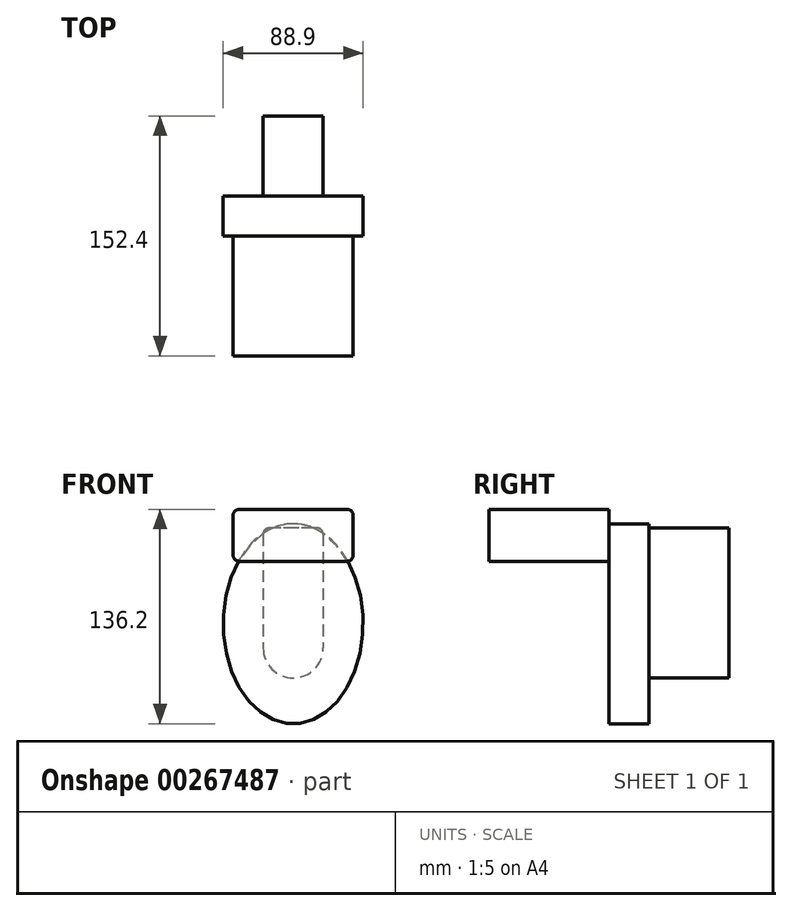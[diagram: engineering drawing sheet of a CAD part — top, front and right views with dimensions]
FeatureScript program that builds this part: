
annotation { "Feature Type Name" : "Feature", "Feature Type Description" : "" }
export const myFeature = defineFeature(function(context is Context, id is Id, definition is map)
    precondition{}
    {
        {
            var Q0;
            Q0=qCreatedBy(makeId("Front.planeOp"),FACE);
            var sketch = newSketch(context, id + "F0", { "sketchPlane" : qUnion([Q0])});
            skLineSegment(sketch, "E0.bottom", {"start": v(15.24, 36.63) * mm, "end": v(-15.24, 36.63) * mm});
            skLineSegment(sketch, "E0.top", {"start": v(19.05, -39.57) * mm, "end": v(-19.05, -39.57) * mm});
            skLineSegment(sketch, "E0.left", {"start": v(19.05, 32.82) * mm, "end": v(19.05, -39.57) * mm});
            skLineSegment(sketch, "E0.right", {"start": v(-19.05, 32.82) * mm, "end": v(-19.05, -39.57) * mm});
            skPoint(sketch, "E0.middle", {"position": v(0, -1.47) * mm});
            skArc(sketch, "E1", {"start": v(-19.05, -39.57) * mm, "mid": v(0, -58.62) * mm, "end": v(19.05, -39.57) * mm});
            skPoint(sketch, "E2.visualSharp", {"position": v(-19.05, 36.63) * mm});
            skArc(sketch, "E2.filletArc", {"start": v(-15.24, 36.63) * mm, "mid": v(-17.93, 35.52) * mm, "end": v(-19.05, 32.82) * mm});
            skPoint(sketch, "E3.visualSharp", {"position": v(19.05, 36.63) * mm});
            skArc(sketch, "E3.filletArc", {"start": v(19.05, 32.82) * mm, "mid": v(17.93, 35.52) * mm, "end": v(15.24, 36.63) * mm});
            skSolve(sketch);
        }
        {
            var Q0;
            Q0=makeQuery(id+"F0.imprint","IMPRINT",FACE,{"disambiguationData":[TD([[makeQuery(id+"F0.imprint","IMPRINT",EDGE,{"derivedFrom":sQuery(id+"F0.wireOp",EDGE,"E0.bottom")}),1.0]])]});
            var Q1;
            Q1=makeQuery(id+"F0.imprint","IMPRINT",FACE,{"disambiguationData":[TD([[makeQuery(id+"F0.imprint","IMPRINT",EDGE,{"derivedFrom":sQuery(id+"F0.wireOp",EDGE,"E0.top")}),1.0]])]});
            extrude(context, id + "F1", {"entities" : qUnion([Q0, Q1]), "depth" : 50.8 * mm});
        }
        {
            var Q0;
            Q0=makeQuery(id+"F1.opExtrude","CAP_FACE",FACE,{"disambiguationData":[OSD([sQuery(id+"F0.wireOp",EDGE,"E0.bottom"),sQuery(id+"F0.wireOp",EDGE,"E0.left"),sQuery(id+"F0.wireOp",EDGE,"E0.right"),sQuery(id+"F0.wireOp",EDGE,"E1"),sQuery(id+"F0.wireOp",EDGE,"E2.filletArc"),sQuery(id+"F0.wireOp",EDGE,"E3.filletArc")])],"isStart":false});
            var sketch = newSketch(context, id + "F2", { "sketchPlane" : qUnion([Q0])});
            skEllipse(sketch, "E4", {"center": v(0, -24.14) * mm, "majorRadius": 63.5 * mm, "minorRadius": 44.45 * mm, "majorAxis": v(0, 1)});
            skSolve(sketch);
        }
        {
            var Q0;
            {var subQ5=makeQuery(id+"F1.opExtrude","CAP_EDGE",EDGE,{"disambiguationData":[OSD([sQuery(id+"F0.wireOp",EDGE,"E1")])],"isStart":false});Q0=makeQuery(id+"F2.imprint","IMPRINT",FACE,{"disambiguationData":[TD([[makeQuery(id+"F2.imprint","IMPRINT",EDGE,{"derivedFrom":subQ5}),-1.0]])]});}
            var Q1;
            {var subQ6=makeQuery(id+"F1.opExtrude","CAP_EDGE",EDGE,{"disambiguationData":[OSD([sQuery(id+"F0.wireOp",EDGE,"E1")])],"isStart":false});Q1=makeQuery(id+"F2.imprint","IMPRINT",FACE,{"disambiguationData":[TD([[makeQuery(id+"F2.imprint","IMPRINT",EDGE,{"derivedFrom":subQ6}),1.0]])]});}
            var Q2;
            {var subQ0=sQuery(id+"F2.wireOp",EDGE,"E4");var subQ1=makeQuery(id+"F1.opExtrude","CAP_EDGE",EDGE,{"disambiguationData":[OSD([sQuery(id+"F0.wireOp",EDGE,"E0.bottom")])],"isStart":false});var subQ2=makeQuery(id+"F2.imprint","INTERSECT",VERTEX,{"disambiguationData":[OD(0.0)],"derivedFrom":[subQ1,subQ0]});Q2=makeQuery(id+"F2.imprint","IMPRINT",FACE,{"disambiguationData":[TD([[makeQuery(id+"F2.imprint","IMPRINT",EDGE,{"disambiguationData":[TD([[subQ2,1.0]])],"derivedFrom":subQ0}),1.0]])]});}
            extrude(context, id + "F3", {"entities" : qUnion([Q0, Q1, Q2]), "operationType" : NewBodyOperationType.ADD, "depth" : 25.4 * mm});
        }
        {
            var Q0;
            Q0=makeQuery(id+"F3.opExtrude","CAP_FACE",FACE,{"disambiguationData":[OSD([sQuery(id+"F2.wireOp",EDGE,"E4")])],"isStart":false});
            var sketch = newSketch(context, id + "F4", { "sketchPlane" : qUnion([Q0])});
            skPoint(sketch, "E5.middle", {"position": v(0, 39.36) * mm});
            skPoint(sketch, "E6.visualSharp", {"position": v(-38.1, 48.56) * mm});
            skPoint(sketch, "E7.visualSharp", {"position": v(38.1, 30.15) * mm});
            skPoint(sketch, "E8.visualSharp", {"position": v(38.1, 48.56) * mm});
            skLineSegment(sketch, "E9.top", {"start": v(-34.29, 15.54) * mm, "end": v(34.29, 15.54) * mm});
            skLineSegment(sketch, "E10", {"start": v(-34.29, 48.56) * mm, "end": v(34.29, 48.56) * mm});
            skArc(sketch, "E11.filletArc", {"start": v(-34.29, 48.56) * mm, "mid": v(-36.98, 47.45) * mm, "end": v(-38.1, 44.75) * mm});
            skPoint(sketch, "E12.visualSharp", {"position": v(-38.1, 15.54) * mm});
            skArc(sketch, "E12.filletArc", {"start": v(-38.1, 19.35) * mm, "mid": v(-36.98, 16.66) * mm, "end": v(-34.29, 15.54) * mm});
            skPoint(sketch, "E13.visualSharp", {"position": v(38.1, 15.54) * mm});
            skArc(sketch, "E13.filletArc", {"start": v(34.29, 15.54) * mm, "mid": v(36.98, 16.66) * mm, "end": v(38.1, 19.35) * mm});
            skArc(sketch, "E14.filletArc", {"start": v(38.1, 44.75) * mm, "mid": v(36.98, 47.45) * mm, "end": v(34.29, 48.56) * mm});
            skLineSegment(sketch, "E15", {"start": v(-38.1, 44.75) * mm, "end": v(-38.1, 19.35) * mm});
            skLineSegment(sketch, "E16", {"start": v(38.1, 19.35) * mm, "end": v(38.1, 44.75) * mm});
            skSolve(sketch);
        }
        {
            var Q0;
            Q0=makeQuery(id+"F4.imprint","IMPRINT",FACE,{"disambiguationData":[TD([[makeQuery(id+"F4.imprint","IMPRINT",EDGE,{"derivedFrom":sQuery(id+"F4.wireOp",EDGE,"E10")}),-1.0]])]});
            var Q1;
            {var subQ0=sQuery(id+"F4.wireOp",EDGE,"E9.top");Q1=makeQuery(id+"F4.imprint","IMPRINT",FACE,{"disambiguationData":[TD([[makeQuery(id+"F4.imprint","IMPRINT",EDGE,{"derivedFrom":subQ0}),1.0]])]});}
            extrude(context, id + "F5", {"entities" : qUnion([Q0, Q1]), "operationType" : NewBodyOperationType.ADD, "depth" : 76.2 * mm});
        }
    });
